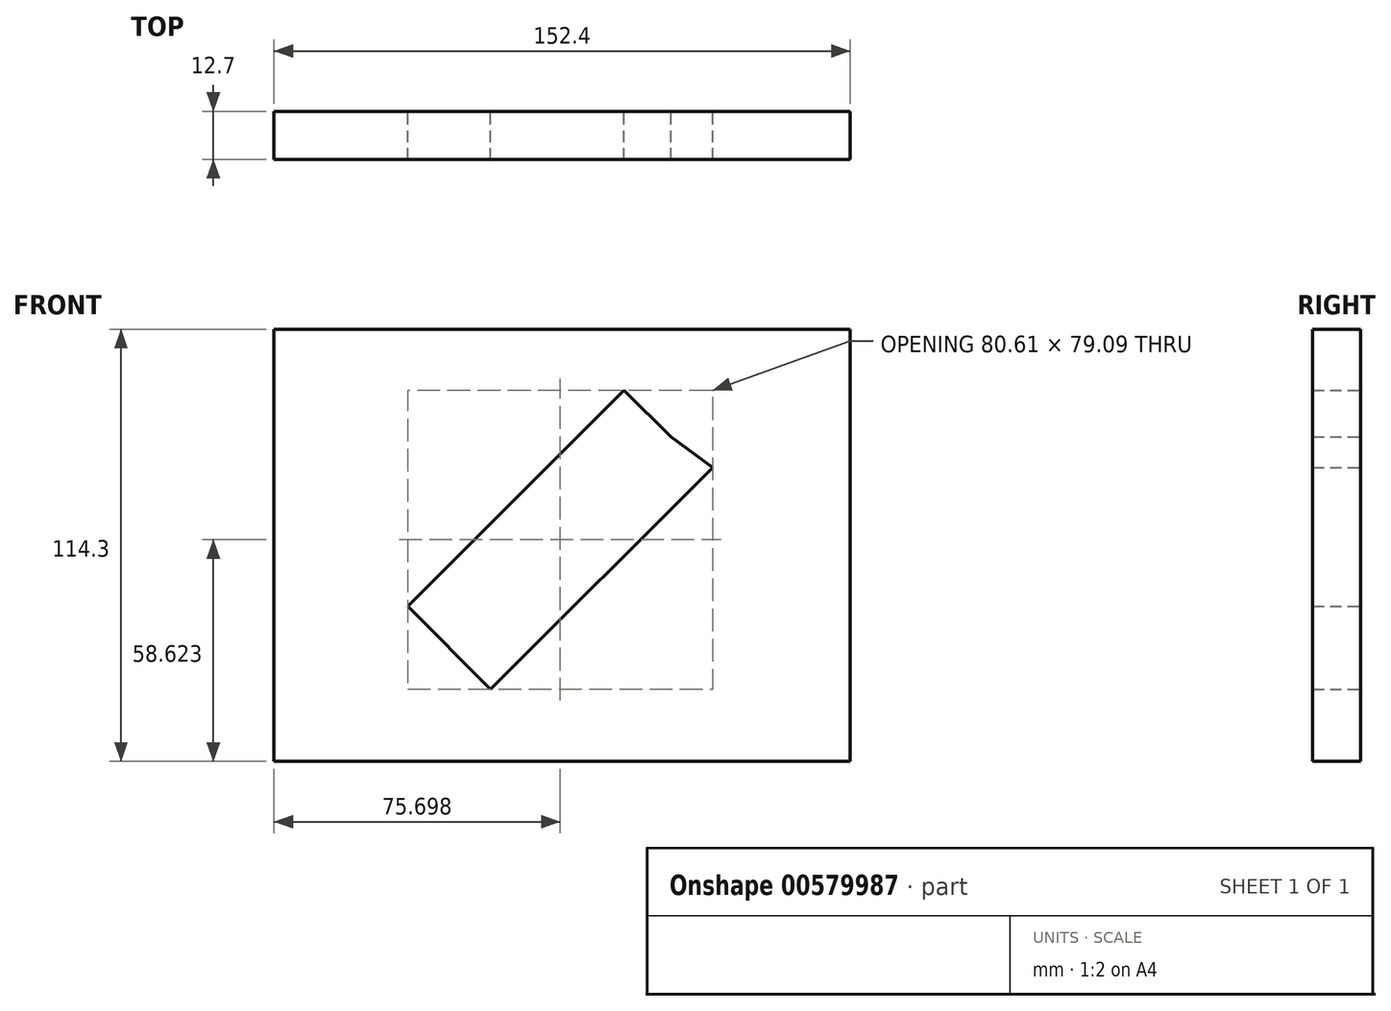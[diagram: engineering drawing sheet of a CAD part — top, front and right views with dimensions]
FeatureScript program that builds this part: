
annotation { "Feature Type Name" : "Feature", "Feature Type Description" : "" }
export const myFeature = defineFeature(function(context is Context, id is Id, definition is map)
    precondition{}
    {
        {
            var Q0;
            Q0=qCreatedBy(makeId("Front.planeOp"),FACE);
            var sketch = newSketch(context, id + "F0", { "sketchPlane" : qUnion([Q0])});
            skLineSegment(sketch, "E0.bottom", {"start": v(-76.2, 57.23) * mm, "end": v(76.2, 57.23) * mm});
            skLineSegment(sketch, "E0.top", {"start": v(-76.2, -57.07) * mm, "end": v(76.2, -57.07) * mm});
            skLineSegment(sketch, "E0.left", {"start": v(-76.2, 57.23) * mm, "end": v(-76.2, -57.07) * mm});
            skLineSegment(sketch, "E0.right", {"start": v(76.2, 57.23) * mm, "end": v(76.2, -57.07) * mm});
            skLineSegment(sketch, "E1", {"start": v(-76.2, 0.08) * mm, "end": v(76.2, 0.08) * mm, "construction": true});
            skLineSegment(sketch, "E2", {"start": v(0, 57.23) * mm, "end": v(0, -57.07) * mm, "construction": true});
            skPoint(sketch, "E3", {"position": v(0, 0) * mm});
            skLineSegment(sketch, "E4", {"start": v(0, 0) * mm, "end": v(-28.74, -28.74) * mm, "construction": true});
            skLineSegment(sketch, "E5", {"start": v(0, 0) * mm, "end": v(28.74, 28.74) * mm, "construction": true});
            skLineSegment(sketch, "E6", {"start": v(28.74, 28.74) * mm, "end": v(16.37, 41.1) * mm});
            skLineSegment(sketch, "E7", {"start": v(16.37, 41.1) * mm, "end": v(-40.8, -16.08) * mm});
            skLineSegment(sketch, "E8", {"start": v(-40.8, -16.08) * mm, "end": v(-18.9, -38) * mm});
            skLineSegment(sketch, "E9", {"start": v(-18.9, -38) * mm, "end": v(39.8, 20.7) * mm});
            skLineSegment(sketch, "E10", {"start": v(39.8, 20.7) * mm, "end": v(28.74, 28.74) * mm});
            skSolve(sketch);
        }
        {
            var Q0;
            Q0 = qSketchRegion(id + "F0", true);
            extrude(context, id + "F1", {"entities" : qUnion([Q0]), "depth" : 12.7 * mm, "offsetDistance" : 25.4 * mm});
        }
    });
